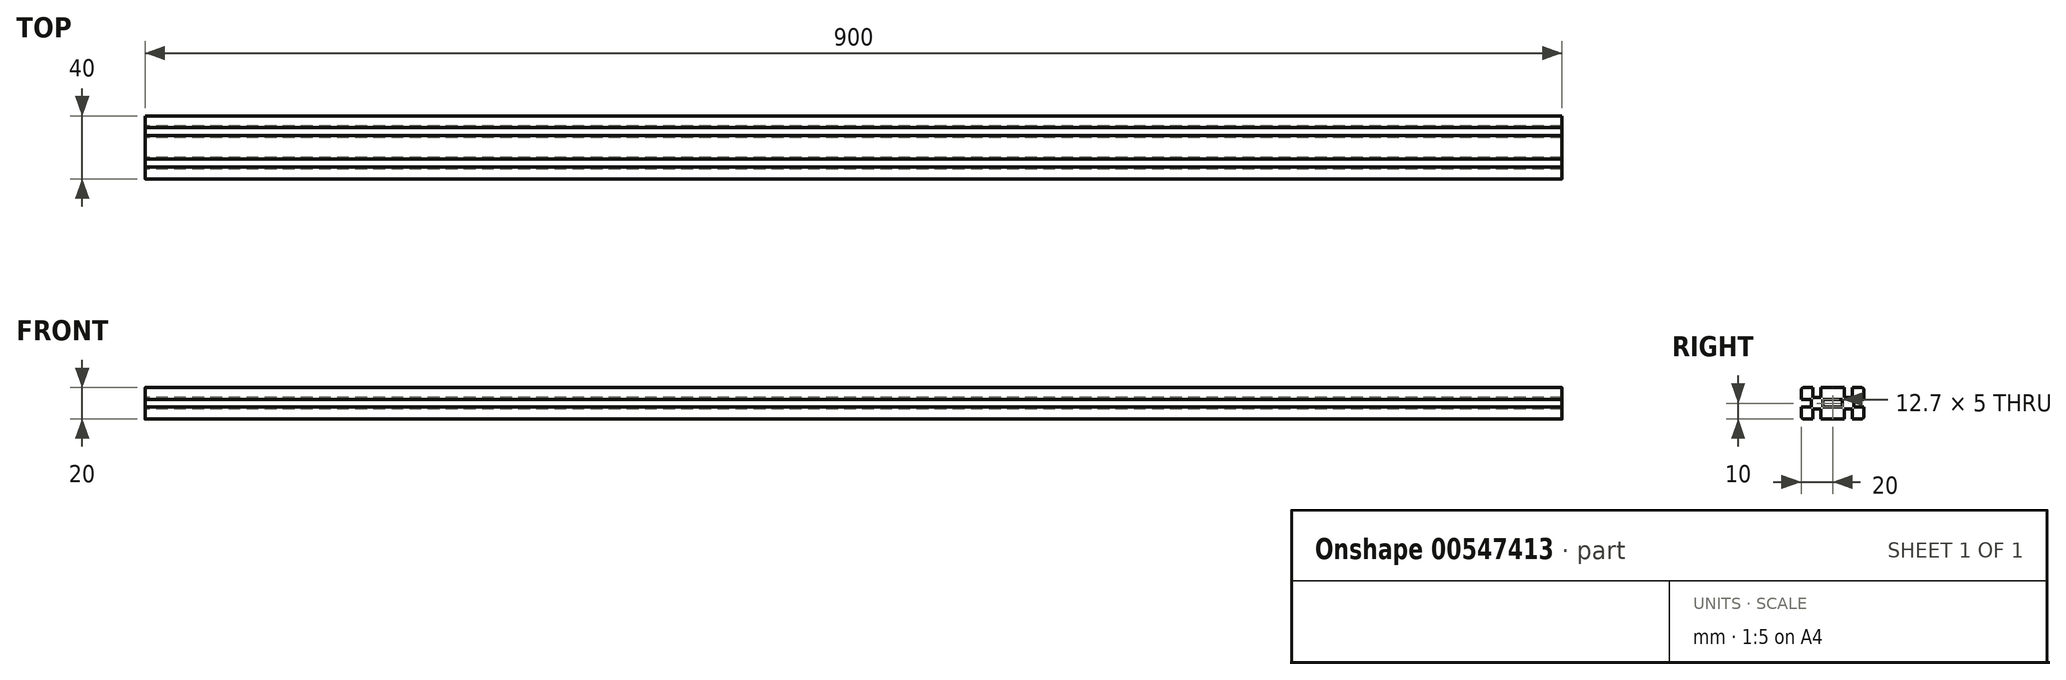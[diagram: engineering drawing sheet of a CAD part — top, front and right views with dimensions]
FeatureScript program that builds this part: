
annotation { "Feature Type Name" : "Feature", "Feature Type Description" : "" }
export const myFeature = defineFeature(function(context is Context, id is Id, definition is map)
    precondition{}
    {
        {
            var Q0;
            Q0=qCreatedBy(makeId("Right.planeOp"),FACE);
            var sketch = newSketch(context, id + "F0", { "sketchPlane" : qUnion([Q0])});
            skLineSegment(sketch, "E0.bottom", {"start": v(20, 10) * mm, "end": v(12.5, 10) * mm});
            skLineSegment(sketch, "E0.top", {"start": v(20, -10) * mm, "end": v(12.5, -10) * mm});
            skLineSegment(sketch, "E0.left", {"start": v(20, 10) * mm, "end": v(20, 2.5) * mm});
            skLineSegment(sketch, "E0.right", {"start": v(-20, 10) * mm, "end": v(-20, 2.5) * mm});
            skPoint(sketch, "E0.middle", {"position": v(0, 0) * mm});
            skLineSegment(sketch, "E1.bottom", {"start": v(-20, 2.5) * mm, "end": v(-13.65, 2.5) * mm});
            skLineSegment(sketch, "E1.top", {"start": v(-20, -2.5) * mm, "end": v(-13.65, -2.5) * mm});
            skLineSegment(sketch, "E1.right", {"start": v(-13.65, 2.5) * mm, "end": v(-13.65, -2.5) * mm});
            skLineSegment(sketch, "E2.top", {"start": v(-12.5, 3.65) * mm, "end": v(-7.5, 3.65) * mm});
            skLineSegment(sketch, "E2.left", {"start": v(-12.5, 10) * mm, "end": v(-12.5, 3.65) * mm});
            skLineSegment(sketch, "E2.right", {"start": v(-7.5, 10) * mm, "end": v(-7.5, 3.65) * mm});
            skLineSegment(sketch, "E3.top", {"start": v(7.5, 3.65) * mm, "end": v(12.5, 3.65) * mm});
            skLineSegment(sketch, "E3.left", {"start": v(7.5, 10) * mm, "end": v(7.5, 3.65) * mm});
            skLineSegment(sketch, "E3.right", {"start": v(12.5, 10) * mm, "end": v(12.5, 3.65) * mm});
            skLineSegment(sketch, "E4.top", {"start": v(-12.5, -3.65) * mm, "end": v(-7.5, -3.65) * mm});
            skLineSegment(sketch, "E4.left", {"start": v(-12.5, -10) * mm, "end": v(-12.5, -3.65) * mm});
            skLineSegment(sketch, "E4.right", {"start": v(-7.5, -10) * mm, "end": v(-7.5, -3.65) * mm});
            skLineSegment(sketch, "E5.top", {"start": v(7.5, -3.65) * mm, "end": v(12.5, -3.65) * mm});
            skLineSegment(sketch, "E5.left", {"start": v(7.5, -10) * mm, "end": v(7.5, -3.65) * mm});
            skLineSegment(sketch, "E5.right", {"start": v(12.5, -10) * mm, "end": v(12.5, -3.65) * mm});
            skLineSegment(sketch, "E6.bottom", {"start": v(20, 2.5) * mm, "end": v(13.65, 2.5) * mm});
            skLineSegment(sketch, "E6.top", {"start": v(20, -2.5) * mm, "end": v(13.65, -2.5) * mm});
            skLineSegment(sketch, "E6.right", {"start": v(13.65, 2.5) * mm, "end": v(13.65, -2.5) * mm});
            skLineSegment(sketch, "E7.trimOffspring", {"start": v(-12.5, 10) * mm, "end": v(-20, 10) * mm});
            skLineSegment(sketch, "E8.trimOffspring", {"start": v(-20, -2.5) * mm, "end": v(-20, -10) * mm});
            skLineSegment(sketch, "E9.trimOffspring", {"start": v(-12.5, -10) * mm, "end": v(-20, -10) * mm});
            skLineSegment(sketch, "E10.trimOffspring", {"start": v(7.5, -10) * mm, "end": v(-7.5, -10) * mm});
            skLineSegment(sketch, "E11.trimOffspring", {"start": v(20, -2.5) * mm, "end": v(20, -10) * mm});
            skLineSegment(sketch, "E12.trimOffspring", {"start": v(7.5, 10) * mm, "end": v(-7.5, 10) * mm});
            skSolve(sketch);
        }
        {
            var Q0;
            Q0 = qSketchRegion(id + "F0", true);
            extrude(context, id + "F1", {"entities" : qUnion([Q0]), "endBound" : BoundingType.SYMMETRIC, "depth" : 900 * mm, "offsetDistance" : 25 * mm});
        }
        {
            var Q0;
            Q0=makeQuery(id+"F1.opExtrude","CAP_FACE",FACE,{"disambiguationData":[OSD([sQuery(id+"F0.wireOp",EDGE,"E0.bottom"),sQuery(id+"F0.wireOp",EDGE,"E0.top"),sQuery(id+"F0.wireOp",EDGE,"E0.left"),sQuery(id+"F0.wireOp",EDGE,"E0.right"),sQuery(id+"F0.wireOp",EDGE,"E1.bottom"),sQuery(id+"F0.wireOp",EDGE,"E1.top"),sQuery(id+"F0.wireOp",EDGE,"E1.right"),sQuery(id+"F0.wireOp",EDGE,"E2.top"),sQuery(id+"F0.wireOp",EDGE,"E2.left"),sQuery(id+"F0.wireOp",EDGE,"E2.right"),sQuery(id+"F0.wireOp",EDGE,"E3.top"),sQuery(id+"F0.wireOp",EDGE,"E3.left"),sQuery(id+"F0.wireOp",EDGE,"E3.right"),sQuery(id+"F0.wireOp",EDGE,"E4.top"),sQuery(id+"F0.wireOp",EDGE,"E4.left"),sQuery(id+"F0.wireOp",EDGE,"E4.right"),sQuery(id+"F0.wireOp",EDGE,"E5.top"),sQuery(id+"F0.wireOp",EDGE,"E5.left"),sQuery(id+"F0.wireOp",EDGE,"E5.right"),sQuery(id+"F0.wireOp",EDGE,"E6.bottom"),sQuery(id+"F0.wireOp",EDGE,"E6.top"),sQuery(id+"F0.wireOp",EDGE,"E6.right"),sQuery(id+"F0.wireOp",EDGE,"E7.trimOffspring"),sQuery(id+"F0.wireOp",EDGE,"E8.trimOffspring"),sQuery(id+"F0.wireOp",EDGE,"E9.trimOffspring"),sQuery(id+"F0.wireOp",EDGE,"E10.trimOffspring"),sQuery(id+"F0.wireOp",EDGE,"E11.trimOffspring"),sQuery(id+"F0.wireOp",EDGE,"E12.trimOffspring")])],"isStart":true});
            var sketch = newSketch(context, id + "F2", { "sketchPlane" : qUnion([Q0])});
            skLineSegment(sketch, "E13.bottom", {"start": v(6.35, 2.5) * mm, "end": v(-6.35, 2.5) * mm});
            skLineSegment(sketch, "E13.top", {"start": v(6.35, -2.5) * mm, "end": v(-6.35, -2.5) * mm});
            skLineSegment(sketch, "E13.left", {"start": v(6.35, 2.5) * mm, "end": v(6.35, -2.5) * mm});
            skLineSegment(sketch, "E13.right", {"start": v(-6.35, 2.5) * mm, "end": v(-6.35, -2.5) * mm});
            skPoint(sketch, "E13.middle", {"position": v(0, 0) * mm});
            skSolve(sketch);
        }
        {
            var Q0;
            Q0 = qSketchRegion(id + "F2", true);
            extrude(context, id + "F3", {"entities" : qUnion([Q0]), "operationType" : NewBodyOperationType.REMOVE, "oppositeDirection" : true, "depth" : 900 * mm, "offsetDistance" : 25 * mm});
        }
        {
            var Q0;
            Q0=makeQuery(id+"F1.opExtrude","SWEPT_EDGE",EDGE,{"disambiguationData":[OSD([sQuery(id+"F0.wireOp",EDGE,"E0.bottom"),sQuery(id+"F0.wireOp",EDGE,"E0.left")])]});
            var Q1;
            Q1=makeQuery(id+"F1.opExtrude","SWEPT_EDGE",EDGE,{"disambiguationData":[OSD([sQuery(id+"F0.wireOp",EDGE,"E8.trimOffspring"),sQuery(id+"F0.wireOp",EDGE,"E9.trimOffspring")])]});
            var Q2;
            Q2=makeQuery(id+"F1.opExtrude","SWEPT_EDGE",EDGE,{"disambiguationData":[OSD([sQuery(id+"F0.wireOp",EDGE,"E0.top"),sQuery(id+"F0.wireOp",EDGE,"E11.trimOffspring")])]});
            var Q3;
            Q3=makeQuery(id+"F1.opExtrude","SWEPT_EDGE",EDGE,{"disambiguationData":[OSD([sQuery(id+"F0.wireOp",EDGE,"E0.right"),sQuery(id+"F0.wireOp",EDGE,"E7.trimOffspring")])]});
            fillet(context, id + "F4", {"entities" : qUnion([Q0, Q1, Q2, Q3]), "radius" : 2 * mm, "tangentPropagation" : true, "allowEdgeOverflow" : false});
        }
    });
